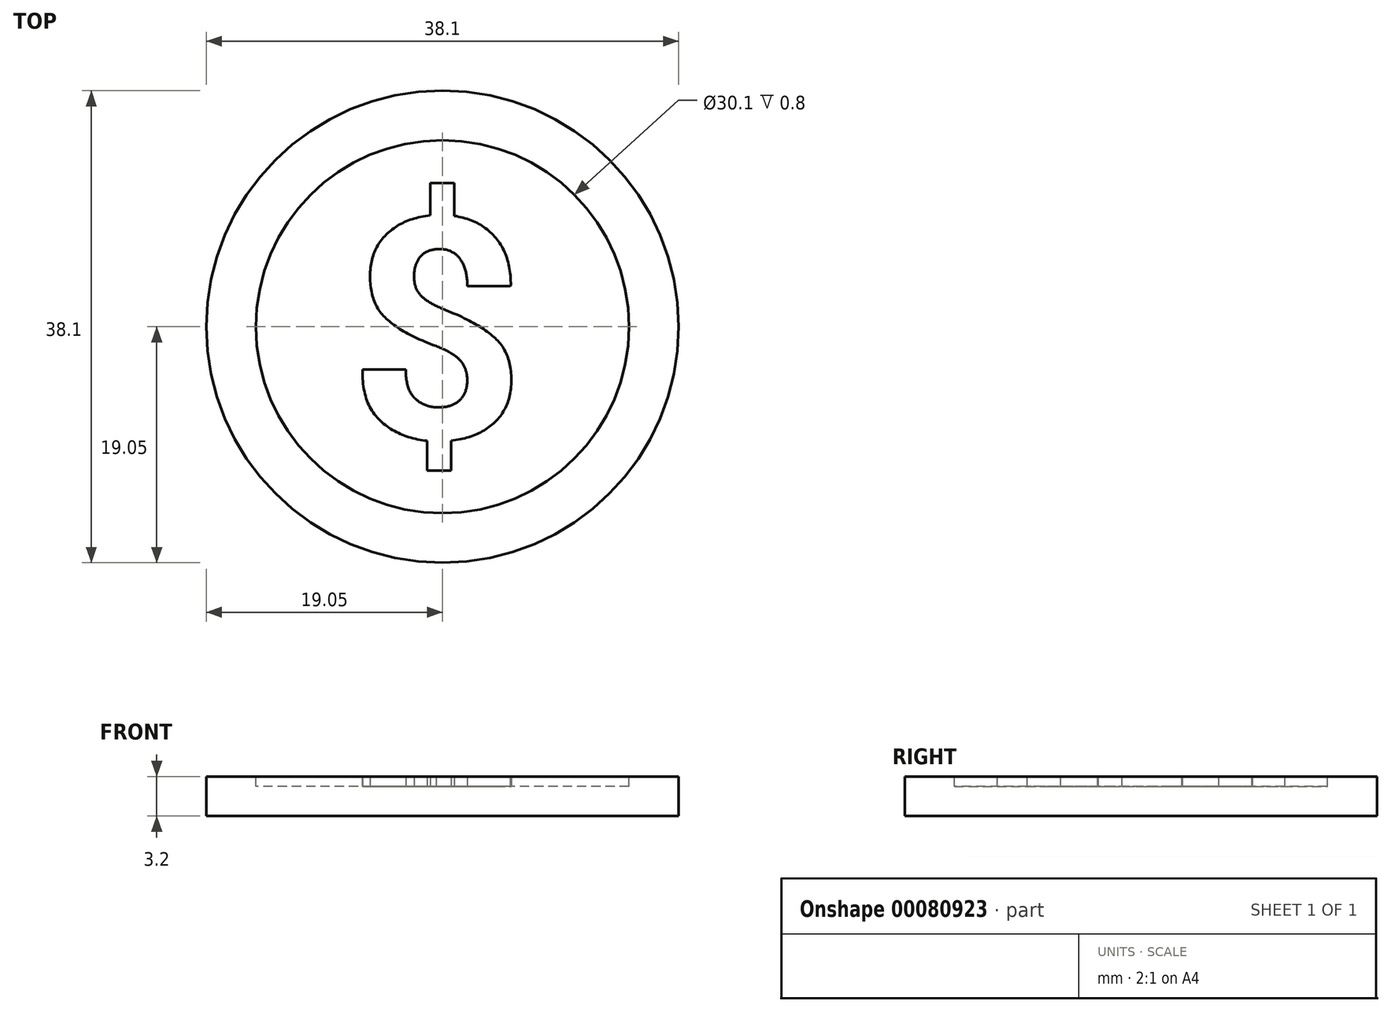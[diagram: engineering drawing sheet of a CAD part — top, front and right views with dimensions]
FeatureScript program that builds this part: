
annotation { "Feature Type Name" : "Feature", "Feature Type Description" : "" }
export const myFeature = defineFeature(function(context is Context, id is Id, definition is map)
    precondition{}
    {
        {
            var Q0;
            Q0=qCreatedBy(makeId("Top.planeOp"),FACE);
            var sketch = newSketch(context, id + "F0", { "sketchPlane" : qUnion([Q0])});
            skCircle(sketch, "E0", {"center": v(0, 0) * mm, "radius": 19.05 * mm});
            skSolve(sketch);
        }
        {
            var Q0;
            Q0 = qSketchRegion(id + "F0", true);
            extrude(context, id + "F1", {"entities" : qUnion([Q0]), "depth" : 3.2 * mm});
        }
        {
            var Q0;
            Q0=makeQuery(id+"F1.opExtrude","CAP_FACE",FACE,{"disambiguationData":[OSD([sQuery(id+"F0.wireOp",EDGE,"E0")])],"isStart":false});
            var sketch = newSketch(context, id + "F2", { "sketchPlane" : qUnion([Q0])});
            skCircle(sketch, "E1", {"center": v(0, 0) * mm, "radius": 15.05 * mm});
            skSolve(sketch);
        }
        {
            var Q0;
            Q0 = qSketchRegion(id + "F2", true);
            extrude(context, id + "F3", {"entities" : qUnion([Q0]), "operationType" : NewBodyOperationType.REMOVE, "oppositeDirection" : true, "depth" : .8 * mm});
        }
        {
            var Q0;
            Q0=makeQuery(id+"F3.boolean.opBoolean","COPY",FACE,{"derivedFrom":makeQuery(id+"F3.opExtrude","CAP_FACE",FACE,{"disambiguationData":[OSD([sQuery(id+"F2.wireOp",EDGE,"E1")])],"isStart":false})});
            var sketch = newSketch(context, id + "F4", { "sketchPlane" : qUnion([Q0])});
            skText(sketch, "E2", { "text": "$", "fontName": "RobotoSlab-Bold.ttf"});
            const initialGuessF4  = {"E2": [-0.00715, -0.009, 1, 0, 0.018]};
            skSetInitialGuess(sketch, initialGuessF4);
            skSolve(sketch);
        }
        {
            var Q0;
            Q0 = qSketchRegion(id + "F4", true);
            extrude(context, id + "F5", {"entities" : qUnion([Q0]), "operationType" : NewBodyOperationType.ADD, "depth" : .8 * mm});
        }
    });
